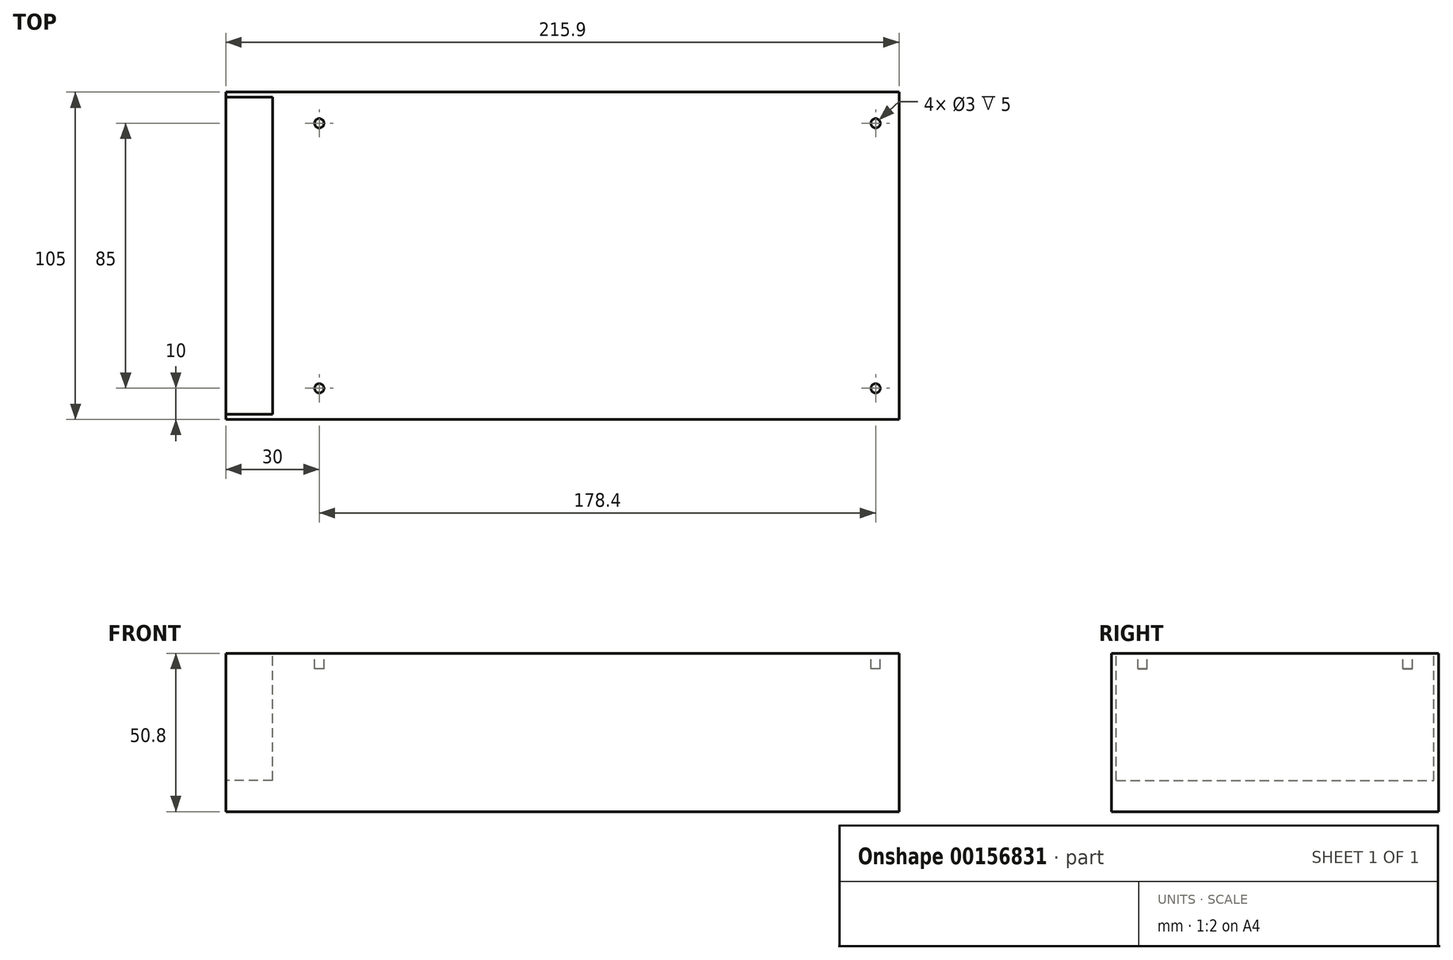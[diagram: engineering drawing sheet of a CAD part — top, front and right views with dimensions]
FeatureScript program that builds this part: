
annotation { "Feature Type Name" : "Feature", "Feature Type Description" : "" }
export const myFeature = defineFeature(function(context is Context, id is Id, definition is map)
    precondition{}
    {
        {
            var Q0;
            Q0=qCreatedBy(makeId("Top.planeOp"),FACE);
            var sketch = newSketch(context, id + "F0", { "sketchPlane" : qUnion([Q0])});
            skLineSegment(sketch, "E0.bottom", {"start": v(107.95, -52.5) * mm, "end": v(-107.95, -52.5) * mm});
            skLineSegment(sketch, "E0.top", {"start": v(107.95, 52.5) * mm, "end": v(-107.95, 52.5) * mm});
            skLineSegment(sketch, "E0.left", {"start": v(107.95, -52.5) * mm, "end": v(107.95, 52.5) * mm});
            skLineSegment(sketch, "E0.right", {"start": v(-107.95, -52.5) * mm, "end": v(-107.95, 52.5) * mm});
            skPoint(sketch, "E0.middle", {"position": v(0, 0) * mm});
            skSolve(sketch);
        }
        {
            var Q0;
            Q0=qSketchRegion(id+"F0",true);
            extrude(context, id + "F1", {"entities" : qUnion([Q0]), "depth" : 50.8 * mm});
        }
        {
            var Q0;
            Q0=makeQuery(id+"F1.opExtrude","CAP_FACE",FACE,{"disambiguationData":[OSD([sQuery(id+"F0.wireOp",EDGE,"E0.bottom"),sQuery(id+"F0.wireOp",EDGE,"E0.top"),sQuery(id+"F0.wireOp",EDGE,"E0.left"),sQuery(id+"F0.wireOp",EDGE,"E0.right")])],"isStart":false});
            var sketch = newSketch(context, id + "F2", { "sketchPlane" : qUnion([Q0])});
            skCircle(sketch, "E1", {"center": v(100.45, 42.5) * mm, "radius": 1.5 * mm});
            skCircle(sketch, "E2", {"center": v(100.45, -42.5) * mm, "radius": 1.5 * mm});
            skCircle(sketch, "E3", {"center": v(-77.95, -42.5) * mm, "radius": 1.5 * mm});
            skCircle(sketch, "E4.MirrorC", {"center": v(-77.95, 42.5) * mm, "radius": 1.5 * mm});
            skSolve(sketch);
        }
        {
            var Q0;
            Q0=qSketchRegion(id+"F2",true);
            extrude(context, id + "F3", {"entities" : qUnion([Q0]), "operationType" : NewBodyOperationType.REMOVE, "oppositeDirection" : true, "depth" : 5 * mm});
        }
        {
            var Q0;
            Q0=makeQuery(id+"F1.opExtrude","CAP_FACE",FACE,{"disambiguationData":[OSD([sQuery(id+"F0.wireOp",EDGE,"E0.bottom"),sQuery(id+"F0.wireOp",EDGE,"E0.top"),sQuery(id+"F0.wireOp",EDGE,"E0.left"),sQuery(id+"F0.wireOp",EDGE,"E0.right")])],"isStart":false});
            var sketch = newSketch(context, id + "F4", { "sketchPlane" : qUnion([Q0])});
            skLineSegment(sketch, "E5.bottom", {"start": v(-92.95, -50.9) * mm, "end": v(-107.95, -50.9) * mm});
            skLineSegment(sketch, "E5.top", {"start": v(-92.95, 50.9) * mm, "end": v(-107.95, 50.9) * mm});
            skLineSegment(sketch, "E5.left", {"start": v(-92.95, -50.9) * mm, "end": v(-92.95, 50.9) * mm});
            skLineSegment(sketch, "E5.right", {"start": v(-107.95, -50.9) * mm, "end": v(-107.95, 50.9) * mm});
            skPoint(sketch, "E5.middle", {"position": v(-100.45, 0) * mm});
            skSolve(sketch);
        }
        {
            var Q0;
            Q0=qSketchRegion(id+"F4",true);
            extrude(context, id + "F5", {"entities" : qUnion([Q0]), "operationType" : NewBodyOperationType.REMOVE, "oppositeDirection" : true, "depth" : 40.8 * mm});
        }
    });
